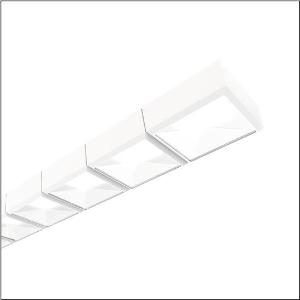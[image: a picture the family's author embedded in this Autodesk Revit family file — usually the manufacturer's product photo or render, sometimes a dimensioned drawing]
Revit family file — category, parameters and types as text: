
# Revit family: scriptus_r__11_5mz323d04wa_1206
name_source: partatom
category: Lighting Fixtures
units: mm (PartAtom-declared; Revit-internal decimal feet)

## family parameters
Cut with Voids When Loaded = No
Host = Face
Light Source = No
Part Type = Normal
Room Calculation Point = No
Round Connector Dimension = Use Diameter
Shared = No

## types (1)
- Scriptus® 11 (1 x LED 4000K / CRI = 80 (unbekannt), 4840 lm / 7230 lm, 4000K)
    Apparent Load = 91 VA
    CIE Flux Codes = - - - 0 100 / 82 95 99 100 100
    Color Rendering = 80
    Color Temperature = 4000K
    Default Elevation = 1800 mm
    Description = Scriptus® 11, office luminaire, primary optical cover: lenses, CAT 2 (L<= 3000cd/m²), light emission: direct/indirect distribution, primary light characteristic: symmetric, installation type: suspended mounting, LED, rated luminous flux: 12.070lm, luminous efficacy: 133lm/W, light colour: 840, colour temperature: 4000K, control gear: ECG DALI, with terminal, 5-pole, mains connection: 230V, AC, 50Hz, rated input power: 91W, LED, control gear: ECG DALI, housing, luminaire housing, of aluminium, traffic white (RAL 9016), length: 2.426mm, width: 114mm, height: 57mm, protection rating (complete): IP20, insulation class (complete): insulation class I (protective earthing), certification: CE, ENEC, VDE, protection symbol: F, permissible operating ambient temperature: 0..+35°C, standard: EN 50419, packaging unit: 1 piece
    Height = 57 mm
    Lamp = 1 x LED 4000K / CRI >= 80 (unbekannt)
    Lamp Light Flux = 4840 lm / 7230 lm
    Lamp count = 1
    Length = 2426 mm
    Luminous efficacy = 133 lm/W
    Manufacturer = Siteco
    ModVariant = No
    Model = 5MZ323D04WA
    Mounting Place = Ceiling
    Mounting Type = Pendant
    Number of Poles = 1
    OnlyDefault = Yes
    Power Factor = 1
    Product Name = Scriptus® 11
    Product group = office luminaire | ceiling pendant
    ProductGroupID = 902
    Protection Class = Protection class I
    Protection Degree = IP 20
    RLX_Detail_Level = 1
    RLX_Emergency_Light_Flux = 0 lm
    RLX_Emergency_Type = 0
    RLX_Emergency_Type_DB = No
    RlxData = <blob elided: 30189 chars, md5=614734aa>
    Socket = socket
    Standby Power = 0 W
    System Light Flux = 12070 lm
    System Power = 91 W
    Type Comments = Product without accessories
    Type Image = l_1004839.jpg
    URL = http://relux.com
    VarID = ---
    Voltage = 0 V
    Weight = 0.00 kg
    Width = 114 mm

## geometry (parser evidence)
native form markers: Blend x4, Sweep x14
no freeform markers — native parametric forms only
